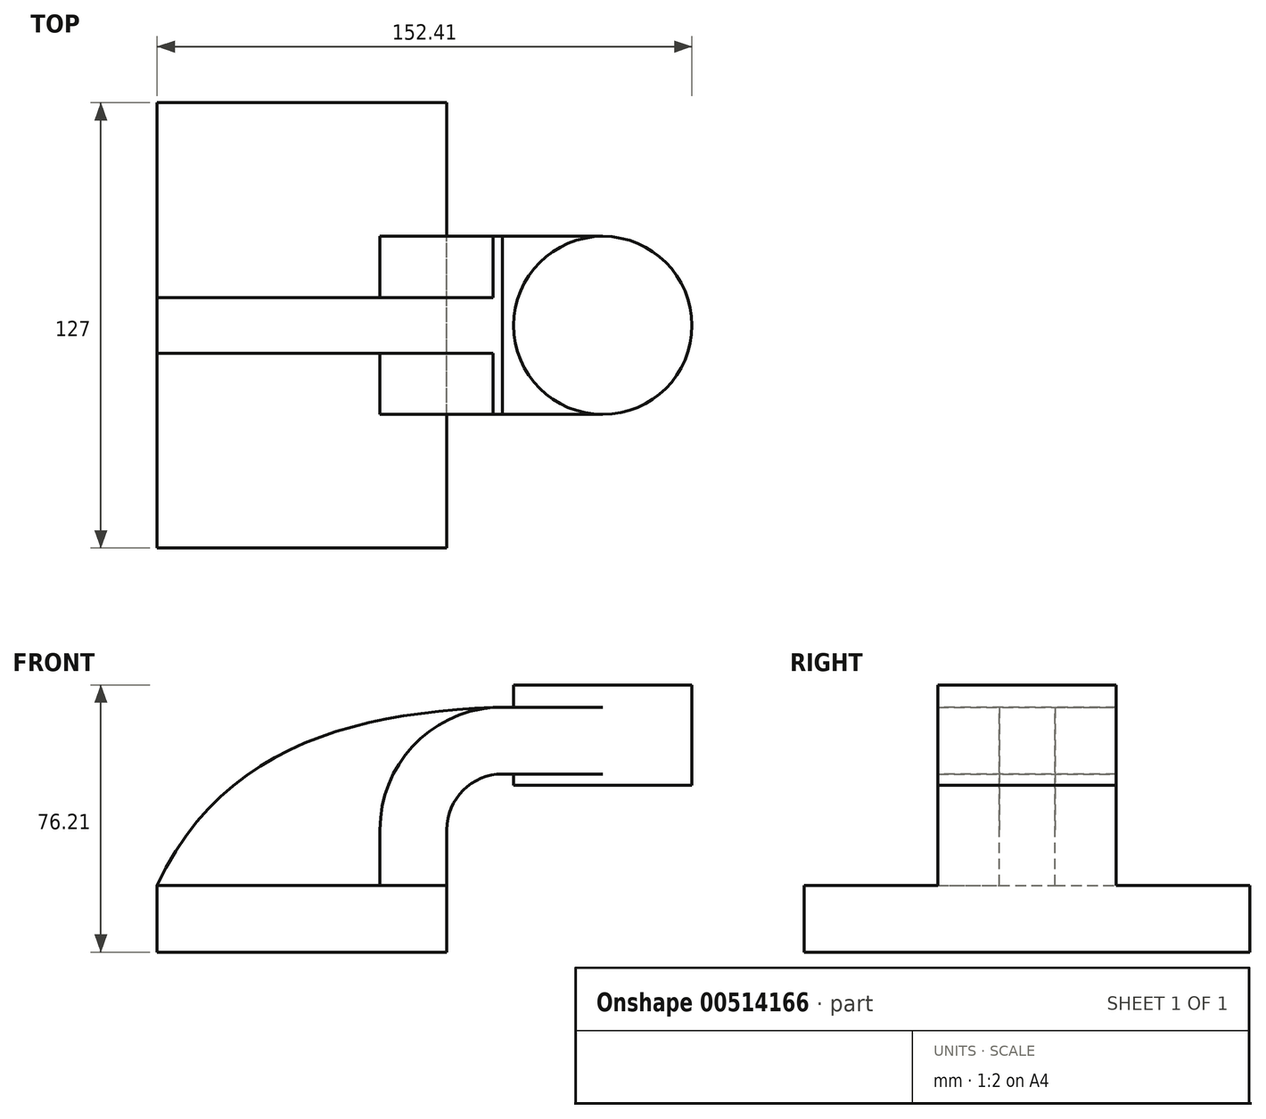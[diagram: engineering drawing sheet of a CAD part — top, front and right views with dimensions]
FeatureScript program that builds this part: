
annotation { "Feature Type Name" : "Feature", "Feature Type Description" : "" }
export const myFeature = defineFeature(function(context is Context, id is Id, definition is map)
    precondition{}
    {
        {
            var Q0;
            Q0=qCreatedBy(makeId("Front.planeOp"),FACE);
            var sketch = newSketch(context, id + "F0", { "sketchPlane" : qUnion([Q0])});
            skLineSegment(sketch, "E0.bottom", {"start": v(-41.27, 9.52) * mm, "end": v(41.28, 9.52) * mm});
            skLineSegment(sketch, "E0.top", {"start": v(-41.27, -9.52) * mm, "end": v(41.27, -9.52) * mm});
            skLineSegment(sketch, "E0.left", {"start": v(-41.27, 9.52) * mm, "end": v(-41.27, -9.52) * mm});
            skLineSegment(sketch, "E0.right", {"start": v(41.27, 9.52) * mm, "end": v(41.27, -9.52) * mm});
            skPoint(sketch, "E0.middle", {"position": v(0, 0) * mm});
            skLineSegment(sketch, "E1.bottom", {"start": v(60.33, 38.1) * mm, "end": v(111.13, 38.1) * mm});
            skLineSegment(sketch, "E1.top", {"start": v(60.33, 66.68) * mm, "end": v(111.13, 66.68) * mm});
            skLineSegment(sketch, "E1.left", {"start": v(60.33, 38.1) * mm, "end": v(60.33, 66.68) * mm});
            skLineSegment(sketch, "E1.right", {"start": v(111.13, 38.1) * mm, "end": v(111.13, 66.68) * mm});
            skPoint(sketch, "E1.middle", {"position": v(85.73, 52.39) * mm});
            skLineSegment(sketch, "E2", {"start": v(41.28, 9.52) * mm, "end": v(41.28, 25.4) * mm});
            skArc(sketch, "E3", {"start": v(41.28, 25.4) * mm, "mid": v(45.92, 36.63) * mm, "end": v(57.15, 41.28) * mm});
            skLineSegment(sketch, "E4", {"start": v(57.15, 41.28) * mm, "end": v(85.73, 41.28) * mm});
            skLineSegment(sketch, "E5.0", {"start": v(57.15, 60.33) * mm, "end": v(85.73, 60.33) * mm});
            skArc(sketch, "E5.1", {"start": v(22.23, 25.4) * mm, "mid": v(32.45, 50.1) * mm, "end": v(57.15, 60.33) * mm});
            skLineSegment(sketch, "E5.2", {"start": v(22.23, 9.52) * mm, "end": v(22.23, 25.4) * mm});
            skLineSegment(sketch, "E6", {"start": v(85.73, 38.1) * mm, "end": v(85.73, 41.28) * mm});
            skLineSegment(sketch, "E7", {"start": v(85.73, 60.33) * mm, "end": v(85.73, 66.68) * mm});
            skLineSegment(sketch, "E8", {"start": v(85.73, 66.68) * mm, "end": v(85.73, 41.28) * mm});
            skFitSpline(sketch, "E9", {"points": [v(-41.27, 9.52) * mm, v(57.15, 60.33) * mm], "startDerivative": vector(56.86, 121.68) * mm, "endDerivative": vector(122.9, 4.21) * mm});
            skSolve(sketch);
        }
        {
            var Q0;
            Q0=makeQuery(id+"F0.imprint","IMPRINT",FACE,{"disambiguationData":[TD([[makeQuery(id+"F0.imprint","IMPRINT",EDGE,{"derivedFrom":sQuery(id+"F0.wireOp",EDGE,"E0.top")}),1.0]])]});
            extrude(context, id + "F1", {"entities" : qUnion([Q0]), "endBound" : BoundingType.SYMMETRIC, "depth" : 127 * mm});
        }
        {
            var Q0;
            {var subQ1=sQuery(id+"F0.wireOp",EDGE,"E2");Q0=makeQuery(id+"F0.imprint","IMPRINT",FACE,{"disambiguationData":[TD([[makeQuery(id+"F0.imprint","IMPRINT",EDGE,{"derivedFrom":subQ1}),1.0]])]});}
            var Q1;
            {var subQ0=sQuery(id+"F0.wireOp",EDGE,"E4");var subQ1=sQuery(id+"F0.wireOp",EDGE,"E1.left");var subQ2=makeQuery(id+"F0.imprint","INTERSECT",VERTEX,{"derivedFrom":[subQ1,subQ0]});Q1=makeQuery(id+"F0.imprint","IMPRINT",FACE,{"disambiguationData":[TD([[makeQuery(id+"F0.imprint","IMPRINT",EDGE,{"disambiguationData":[TD([[subQ2,-1.0]])],"derivedFrom":subQ1}),-1.0]])]});}
            extrude(context, id + "F2", {"entities" : qUnion([Q0, Q1]), "operationType" : NewBodyOperationType.ADD, "endBound" : BoundingType.SYMMETRIC, "depth" : 50.8 * mm});
        }
        {
            var Q0;
            {var subQ3=sQuery(id+"F0.wireOp",EDGE,"E5.2");Q0=makeQuery(id+"F0.imprint","IMPRINT",FACE,{"disambiguationData":[TD([[makeQuery(id+"F0.imprint","IMPRINT",EDGE,{"derivedFrom":subQ3}),1.0]])]});}
            extrude(context, id + "F3", {"entities" : qUnion([Q0]), "operationType" : NewBodyOperationType.ADD, "endBound" : BoundingType.SYMMETRIC, "depth" : 15.88 * mm});
        }
        {
            var Q0;
            {var subQ1=sQuery(id+"F0.wireOp",EDGE,"E1.right");Q0=makeQuery(id+"F0.imprint","IMPRINT",FACE,{"disambiguationData":[TD([[makeQuery(id+"F0.imprint","IMPRINT",EDGE,{"derivedFrom":subQ1}),1.0]])]});}
            var Q1;
            Q1=sQuery(id+"F0.wireOp",EDGE,"E8");
            revolve(context, id + "F4", {"operationType" : NewBodyOperationType.ADD, "entities" : qUnion([Q0]), "axis" : qUnion([Q1]), "revolveType" : RevolveType.FULL});
        }
    });
